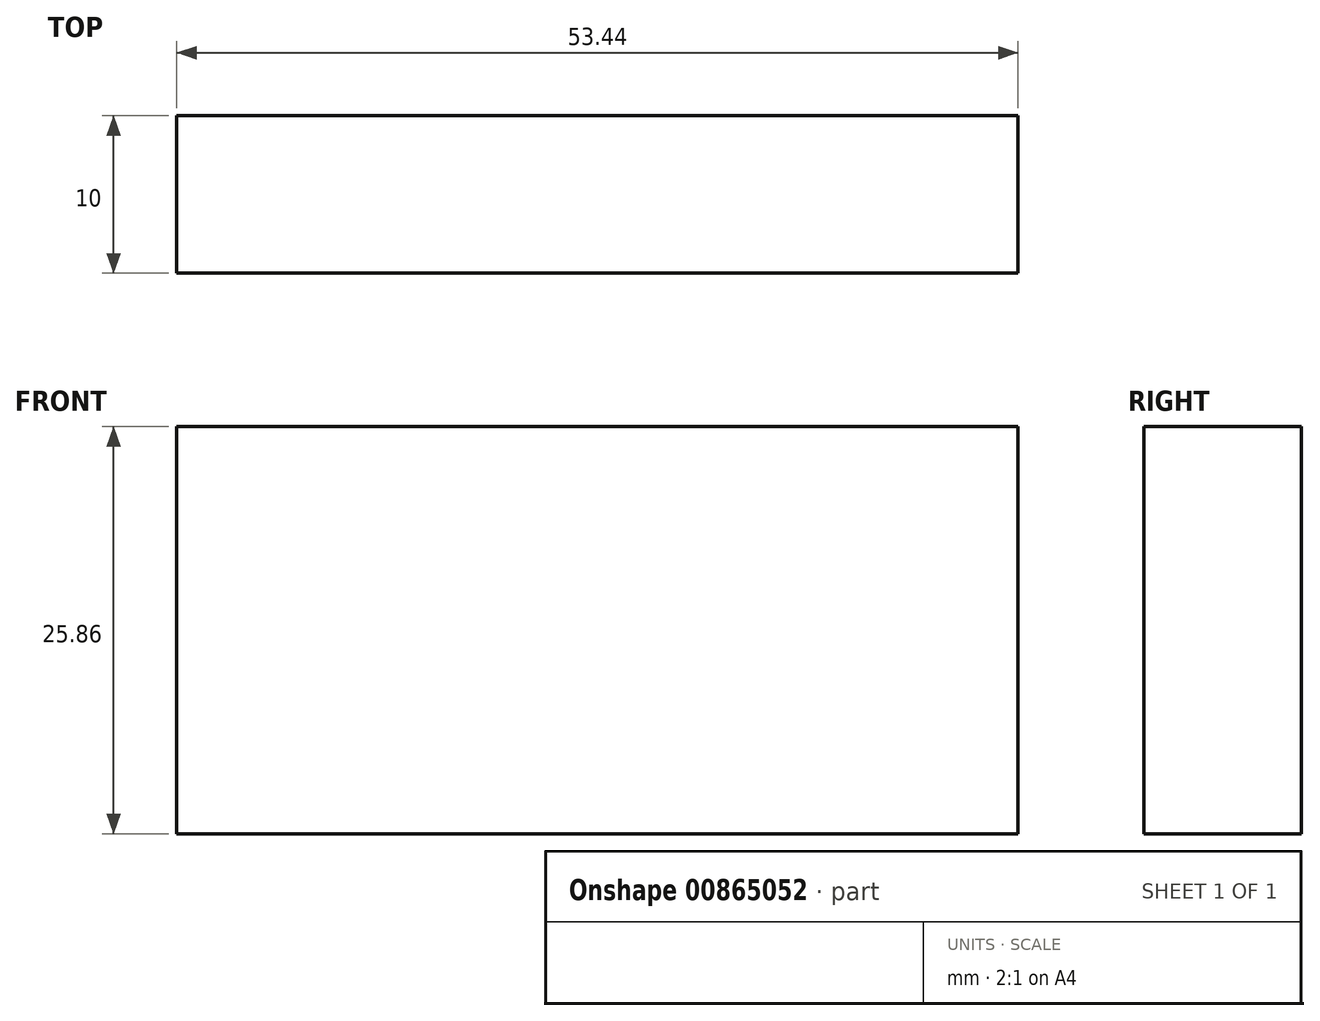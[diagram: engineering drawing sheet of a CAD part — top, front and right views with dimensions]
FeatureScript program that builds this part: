
annotation { "Feature Type Name" : "Feature", "Feature Type Description" : "" }
export const myFeature = defineFeature(function(context is Context, id is Id, definition is map)
    precondition{}
    {
        {
            var Q0;
            Q0=qCreatedBy(makeId("Front.planeOp"),FACE);
            var sketch = newSketch(context, id + "F0", { "sketchPlane" : qUnion([Q0])});
            skLineSegment(sketch, "E0.bottom", {"start": v(0, 0) * mm, "end": v(53.44, 0) * mm});
            skLineSegment(sketch, "E0.top", {"start": v(0, 25.86) * mm, "end": v(53.44, 25.86) * mm});
            skLineSegment(sketch, "E0.left", {"start": v(0, 0) * mm, "end": v(0, 25.86) * mm});
            skLineSegment(sketch, "E0.right", {"start": v(53.44, 0) * mm, "end": v(53.44, 25.86) * mm});
            skSolve(sketch);
        }
        {
            var Q0;
            Q0=makeQuery(id+"F0.imprint","IMPRINT",FACE,{"disambiguationData":[TD([[makeQuery(id+"F0.imprint","IMPRINT",EDGE,{"derivedFrom":sQuery(id+"F0.wireOp",EDGE,"E0.bottom")}),1.0]])]});
            extrude(context, id + "F1", {"entities" : qUnion([Q0]), "oppositeDirection" : true, "depth" : 10 * mm, "offsetDistance" : 25 * mm});
        }
    });
